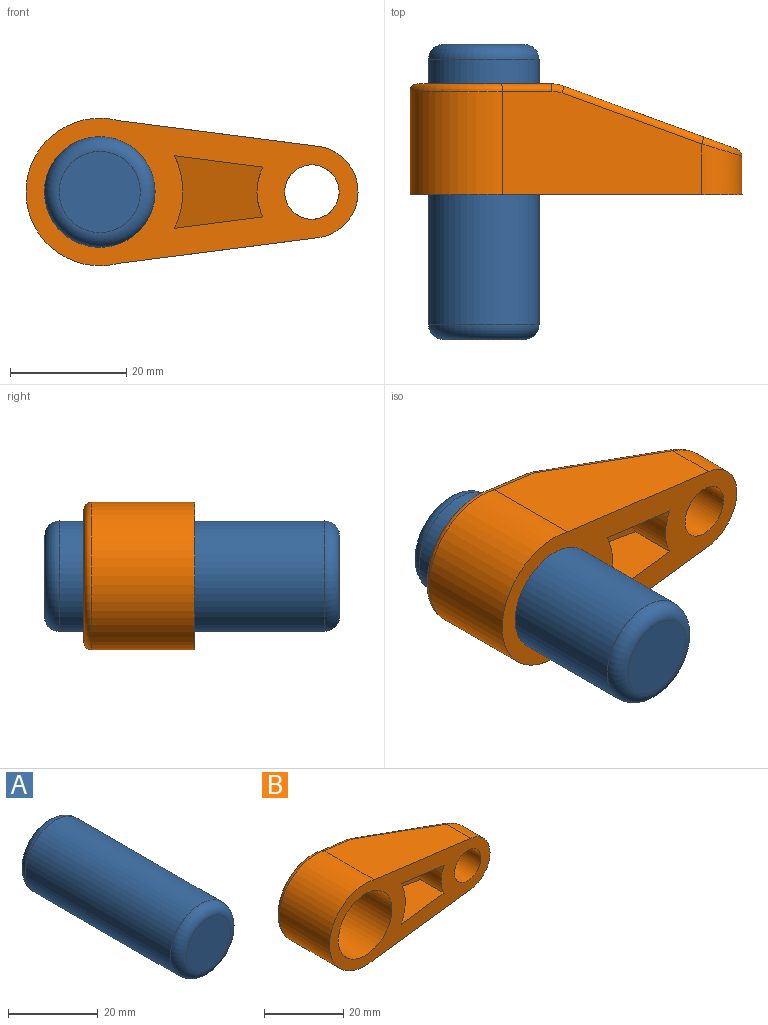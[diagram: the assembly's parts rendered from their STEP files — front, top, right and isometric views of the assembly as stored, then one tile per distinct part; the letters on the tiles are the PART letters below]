
ASSEMBLY  parts=2 mates=1
PART A: 5 faces, bbox 20.6x50.8x20.6 mm
  f0: cylinder r=9.53mm len=45.72mm, axis (0,1,0), area 2736.2mm2, adj f3,f4
  f1: plane 13.97x13.97mm, normal (0,-1,0), area 153.3mm2, adj f4
  f2: plane 13.97x13.97mm, normal (0,1,0), area 153.3mm2, adj f3
  f3: torus R=6.99mm, axis (0,-1,0), area 215.6mm2, adj f0,f2
  f4: torus R=6.99mm, axis (0,-1,0), area 215.6mm2, adj f0,f1
PART B: 23 faces, bbox 58.2x19.1x27.5 mm
  f0: plane 57.15x25.4mm, normal (0,-1,0), area 612.2mm2, adj f1,f2,f3,f4,f5,f6,f18,f19
  f1: plane 34.31x17.78mm, normal (0.13,0,-0.99), area 501.4mm2, adj f0,f2,f5,f14,f16,f17
  f2: cylinder r=7.94mm len=15.75mm, axis (0,1,0), area 168.7mm2, adj f0,f1,f4,f12
  f3: cylinder r=4.69mm len=12.09mm, axis (0,1,0), area 306mm2, adj f0,f8
  f4: plane 34.31x17.78mm, normal (0.13,0,0.99), area 501.4mm2, adj f0,f2,f5,f10,f11,f13
  f5: cylinder r=12.7mm len=25.4mm, axis (0,1,0), area 824.9mm2, adj f0,f1,f4,f15
  f6: cylinder r=9.53mm len=19.05mm, axis (0,1,0), area 1140.1mm2, adj f0,f7
  f7: plane 23.01x22.86mm, normal (0,1,0), area 167.9mm2, adj f6,f9,f13,f15,f17
  f8: plane 29.86x19.41mm, normal (0.34,0.94,0), area 406.3mm2, adj f3,f9,f10,f12,f14
  f9: cylinder r=6.35mm len=19.86mm, axis (0,0,1), area 43.5mm2, adj f7,f8,f11,f16
  f10: cylinder r=1.27mm len=24.34mm, axis (-0.93,0.34,0.12), area 50mm2, adj f4,f8,f11,f12
  f11: bspline ~3.92x1.75mm, area 4.1mm2, adj f4,f9,f10,f13
  f12: bspline ~15.75x6.92mm, area 37.1mm2, adj f2,f8,f10,f14
  f13: cylinder r=1.27mm len=8.77mm, axis (-0.99,0,0.13), area 17.2mm2, adj f4,f7,f11,f15
  f14: cylinder r=1.27mm len=24.34mm, axis (0.93,-0.34,0.12), area 50mm2, adj f1,f8,f12,f16
  f15: torus R=11.43mm, axis (0,-1,0), area 89.4mm2, adj f5,f7,f13,f17
  f16: bspline ~3.92x1.75mm, area 4.1mm2, adj f1,f9,f14,f17
  f17: cylinder r=1.27mm len=8.77mm, axis (0.99,0,0.13), area 17.2mm2, adj f1,f7,f15,f16
  f18: plane 15.24x13.93mm, normal (-0.13,0,0.99), area 171.4mm2, adj f0,f19,f21,f22
  f19: cylinder r=9.45mm len=8.76mm, axis (0,1,0), area 76.8mm2, adj f0,f18,f20,f22
  f20: plane 15.24x13.93mm, normal (-0.13,0,-0.99), area 171.4mm2, adj f0,f19,f21,f22
  f21: cylinder r=14.29mm len=13.93mm, axis (0,1,0), area 175.5mm2, adj f0,f18,f20,f22
  f22: plane 15.24x12.49mm, normal (-0.34,-0.94,0), area 151.6mm2, adj f18,f19,f20,f21
PLACE A t=(-0.35,0,156.94)mm
PLACE B t=(-0.35,-6.8,156.94)mm
MATE cylindrical B.f6 <-> A.f0  axis (0,1,0) through (-0.35,-6.8,156.94)mm
